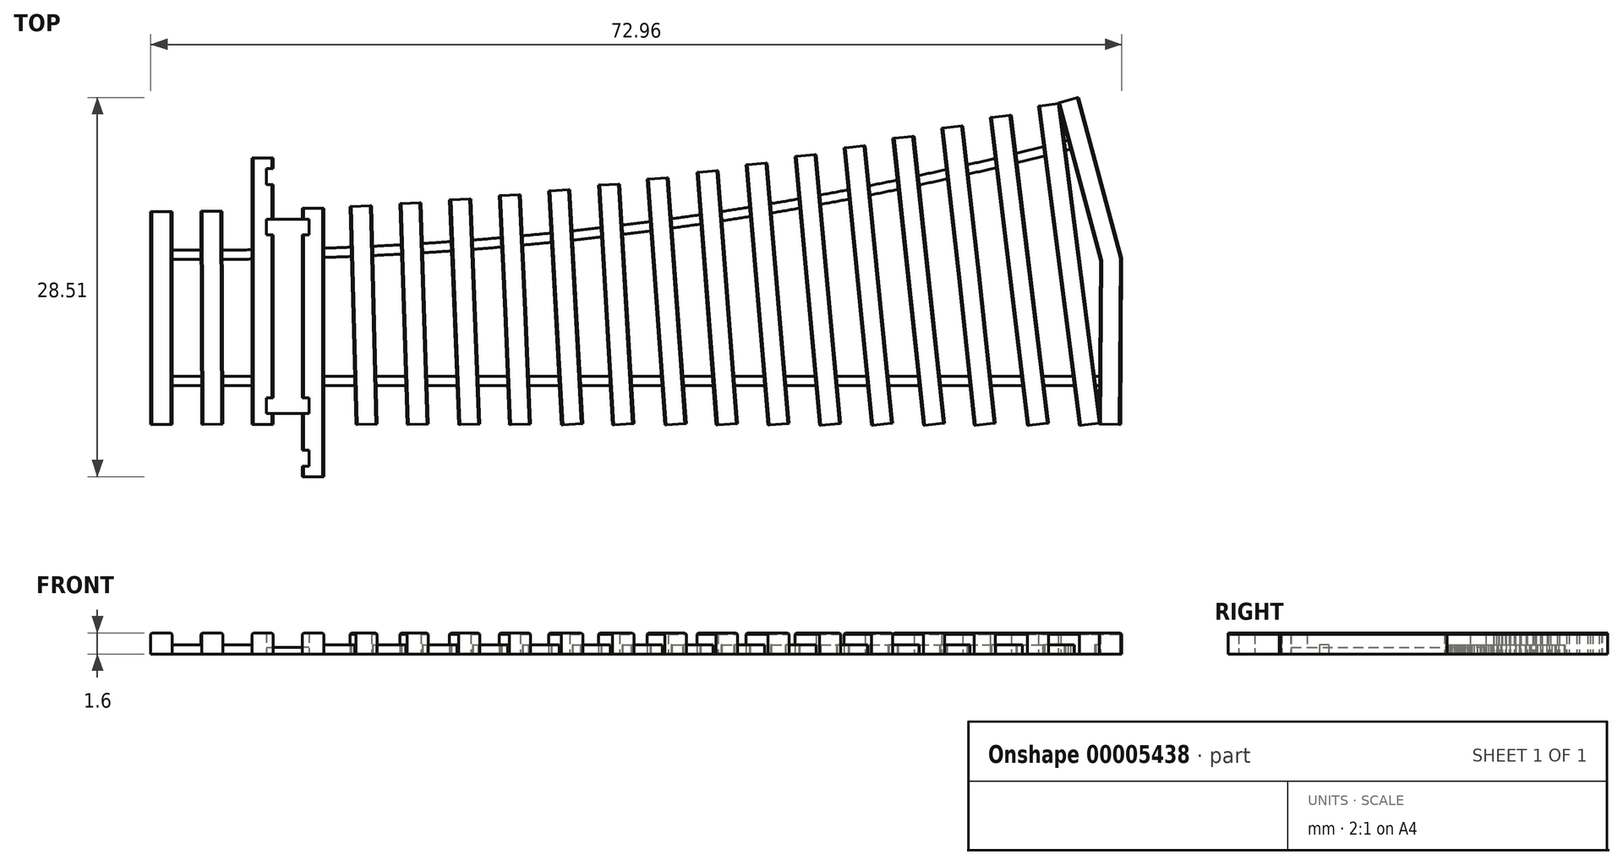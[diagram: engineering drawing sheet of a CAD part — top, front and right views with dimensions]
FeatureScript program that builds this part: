
annotation { "Feature Type Name" : "Feature", "Feature Type Description" : "" }
export const myFeature = defineFeature(function(context is Context, id is Id, definition is map)
    precondition{}
    {
        {
            var Q0;
            Q0=qCreatedBy(makeId("Top.planeOp"),FACE);
            var sketch = newSketch(context, id + "F0", { "sketchPlane" : qUnion([Q0])});
            skLineSegment(sketch, "E0", {"start": v(0, 0) * mm, "end": v(0, 4.5) * mm, "construction": true});
            skLineSegment(sketch, "E1", {"start": v(0, 4.5) * mm, "end": v(-1.16, 8.85) * mm, "construction": true});
            skLineSegment(sketch, "E2", {"start": v(-1.16, 8.85) * mm, "end": v(-34.18, 0) * mm, "construction": true});
            skLineSegment(sketch, "E3", {"start": v(-34.18, 0) * mm, "end": v(0, 0) * mm, "construction": true});
            skLineSegment(sketch, "E4", {"start": v(-34.18, 0) * mm, "end": v(-34.18, 4.5) * mm, "construction": true});
            skLineSegment(sketch, "E5.0.MirrorCS", {"start": v(-34.18, 0) * mm, "end": v(-68.36, 0) * mm, "construction": true});
            skLineSegment(sketch, "E6.0.MirrorCS", {"start": v(0, 0) * mm, "end": v(0, -4.5) * mm, "construction": true});
            skLineSegment(sketch, "E7", {"start": v(0, -4.5) * mm, "end": v(-68.36, -4.5) * mm, "construction": true});
            skLineSegment(sketch, "E8.0.MirrorCS", {"start": v(-2.33, 13.2) * mm, "end": v(-1.16, 8.85) * mm, "construction": true});
            skLineSegment(sketch, "E9", {"start": v(-68.36, 0) * mm, "end": v(-68.36, -4.5) * mm, "construction": true});
            skLineSegment(sketch, "E10.0.MirrorCS", {"start": v(-68.36, 0) * mm, "end": v(-68.36, 4.5) * mm, "construction": true});
            skLineSegment(sketch, "E11", {"start": v(-68.36, 0) * mm, "end": v(-71.36, 0) * mm, "construction": true});
            skArc(sketch, "E12", {"start": v(-68.36, 0) * mm, "mid": v(-34.47, 2.22) * mm, "end": v(-1.16, 8.85) * mm, "construction": true});
            skLineSegment(sketch, "E13", {"start": v(-68.36, -4.5) * mm, "end": v(-71.36, -4.5) * mm, "construction": true});
            skLineSegment(sketch, "E14", {"start": v(-68.36, 4.5) * mm, "end": v(-71.36, 4.5) * mm, "construction": true});
            skArc(sketch, "E15", {"start": v(-68.36, 4.5) * mm, "mid": v(-35.06, 6.68) * mm, "end": v(-2.33, 13.2) * mm, "construction": true});
            skSolve(sketch);
        }
        {
            var Q0;
            Q0=qCreatedBy(makeId("Top.planeOp"),FACE);
            var sketch = newSketch(context, id + "F1", { "sketchPlane" : qUnion([Q0])});
            skPoint(sketch, "E16.0", {"position": v(-68.36, 0) * mm});
            skLineSegment(sketch, "E17.0", {"start": v(-68.36, 0) * mm, "end": v(-72.16, 0) * mm, "construction": true});
            skArc(sketch, "E18", {"start": v(-68.36, 0) * mm, "mid": v(-34.1, 1.13) * mm, "end": v(0, 4.5) * mm, "construction": true});
            skLineSegment(sketch, "E19", {"start": v(-68.36, 0) * mm, "end": v(-64.56, 0.01) * mm, "construction": true});
            skLineSegment(sketch, "E20", {"start": v(-64.56, 0.01) * mm, "end": v(-60.76, 0.06) * mm, "construction": true});
            skLineSegment(sketch, "E21", {"start": v(-60.76, 0.06) * mm, "end": v(-56.96, 0.12) * mm, "construction": true});
            skLineSegment(sketch, "E22", {"start": v(-56.96, 0.12) * mm, "end": v(-53.16, 0.22) * mm, "construction": true});
            skLineSegment(sketch, "E23", {"start": v(-53.16, 0.22) * mm, "end": v(-49.37, 0.35) * mm, "construction": true});
            skLineSegment(sketch, "E24", {"start": v(-49.37, 0.35) * mm, "end": v(-45.57, 0.5) * mm, "construction": true});
            skLineSegment(sketch, "E25", {"start": v(-45.57, 0.5) * mm, "end": v(-41.77, 0.68) * mm, "construction": true});
            skLineSegment(sketch, "E26", {"start": v(-41.77, 0.68) * mm, "end": v(-37.98, 0.89) * mm, "construction": true});
            skLineSegment(sketch, "E27", {"start": v(-37.98, 0.89) * mm, "end": v(-34.19, 1.1) * mm, "construction": true});
            skLineSegment(sketch, "E28", {"start": v(-34.19, 1.1) * mm, "end": v(-30.4, 1.38) * mm, "construction": true});
            skLineSegment(sketch, "E29", {"start": v(-30.4, 1.38) * mm, "end": v(-26.6, 1.67) * mm, "construction": true});
            skLineSegment(sketch, "E30", {"start": v(-26.6, 1.67) * mm, "end": v(-22.82, 2) * mm, "construction": true});
            skLineSegment(sketch, "E31", {"start": v(-22.82, 2) * mm, "end": v(-19.04, 2.34) * mm, "construction": true});
            skLineSegment(sketch, "E32", {"start": v(-19.04, 2.34) * mm, "end": v(-15.25, 2.71) * mm, "construction": true});
            skLineSegment(sketch, "E33", {"start": v(-15.25, 2.71) * mm, "end": v(-11.48, 3.11) * mm, "construction": true});
            skLineSegment(sketch, "E34", {"start": v(-11.48, 3.11) * mm, "end": v(-7.7, 3.54) * mm, "construction": true});
            skLineSegment(sketch, "E35", {"start": v(-7.7, 3.54) * mm, "end": v(-3.93, 4) * mm, "construction": true});
            skLineSegment(sketch, "E36", {"start": v(-3.93, 4) * mm, "end": v(-0.16, 4.48) * mm, "construction": true});
            skLineSegment(sketch, "E37", {"start": v(-72.16, 0) * mm, "end": v(-72.16, 8) * mm, "construction": true});
            skLineSegment(sketch, "E38", {"start": v(-68.36, 0) * mm, "end": v(-68.4, 8.03) * mm, "construction": true});
            skLineSegment(sketch, "E39", {"start": v(-56.96, 0.12) * mm, "end": v(-57.17, 8.4) * mm, "construction": true});
            skLineSegment(sketch, "E40", {"start": v(-53.16, 0.22) * mm, "end": v(-53.44, 8.62) * mm, "construction": true});
            skLineSegment(sketch, "E41", {"start": v(-49.37, 0.35) * mm, "end": v(-49.7, 8.9) * mm, "construction": true});
            skLineSegment(sketch, "E42", {"start": v(-45.57, 0.5) * mm, "end": v(-45.98, 9.22) * mm, "construction": true});
            skLineSegment(sketch, "E43", {"start": v(-41.77, 0.68) * mm, "end": v(-42.26, 9.6) * mm, "construction": true});
            skLineSegment(sketch, "E44", {"start": v(-37.98, 0.89) * mm, "end": v(-38.51, 10.02) * mm, "construction": true});
            skLineSegment(sketch, "E45", {"start": v(-34.19, 1.1) * mm, "end": v(-34.87, 10.48) * mm, "construction": true});
            skLineSegment(sketch, "E46", {"start": v(-30.4, 1.38) * mm, "end": v(-31.13, 11) * mm, "construction": true});
            skLineSegment(sketch, "E47", {"start": v(-26.6, 1.67) * mm, "end": v(-27.44, 11.58) * mm, "construction": true});
            skLineSegment(sketch, "E48", {"start": v(-22.82, 2) * mm, "end": v(-23.75, 12.2) * mm, "construction": true});
            skLineSegment(sketch, "E49", {"start": v(-19.04, 2.34) * mm, "end": v(-20.07, 12.86) * mm, "construction": true});
            skLineSegment(sketch, "E50", {"start": v(-15.25, 2.71) * mm, "end": v(-16.4, 13.58) * mm, "construction": true});
            skLineSegment(sketch, "E51", {"start": v(-11.48, 3.11) * mm, "end": v(-12.75, 14.34) * mm, "construction": true});
            skLineSegment(sketch, "E52", {"start": v(-7.7, 3.54) * mm, "end": v(-9.1, 15.16) * mm, "construction": true});
            skLineSegment(sketch, "E53", {"start": v(-3.93, 4) * mm, "end": v(-5.47, 16.02) * mm, "construction": true});
            skLineSegment(sketch, "E54", {"start": v(-72.16, 8) * mm, "end": v(-73.88, 8) * mm});
            skLineSegment(sketch, "E55.0.MirrorCS", {"start": v(-72.16, 0) * mm, "end": v(-72.16, -8) * mm, "construction": true});
            skLineSegment(sketch, "E56", {"start": v(-72.16, -8) * mm, "end": v(-2.39, -8) * mm, "construction": true});
            skLineSegment(sketch, "E57", {"start": v(-68.36, 0) * mm, "end": v(-68.33, -8) * mm, "construction": true});
            skLineSegment(sketch, "E58", {"start": v(-60.76, 0.06) * mm, "end": v(-60.76, 8.23) * mm, "construction": true});
            skLineSegment(sketch, "E59", {"start": v(-60.76, 0.06) * mm, "end": v(-60.76, -11.94) * mm, "construction": true});
            skLineSegment(sketch, "E60", {"start": v(-64.56, 0.01) * mm, "end": v(-64.56, 12.01) * mm, "construction": true});
            skLineSegment(sketch, "E61", {"start": v(-56.96, 0.12) * mm, "end": v(-56.76, -8) * mm, "construction": true});
            skLineSegment(sketch, "E62", {"start": v(-53.16, 0.22) * mm, "end": v(-52.9, -8) * mm, "construction": true});
            skLineSegment(sketch, "E63", {"start": v(-49.37, 0.35) * mm, "end": v(-49.03, -8) * mm, "construction": true});
            skLineSegment(sketch, "E64", {"start": v(-45.57, 0.5) * mm, "end": v(-45.23, -8) * mm, "construction": true});
            skLineSegment(sketch, "E65", {"start": v(-41.77, 0.68) * mm, "end": v(-41.3, -8) * mm, "construction": true});
            skLineSegment(sketch, "E66", {"start": v(-37.98, 0.89) * mm, "end": v(-37.46, -8) * mm, "construction": true});
            skLineSegment(sketch, "E67", {"start": v(-34.19, 1.1) * mm, "end": v(-33.52, -8) * mm, "construction": true});
            skLineSegment(sketch, "E68", {"start": v(-30.4, 1.38) * mm, "end": v(-29.68, -8) * mm, "construction": true});
            skLineSegment(sketch, "E69", {"start": v(-26.6, 1.67) * mm, "end": v(-25.8, -8) * mm, "construction": true});
            skLineSegment(sketch, "E70", {"start": v(-22.82, 2) * mm, "end": v(-21.9, -8) * mm, "construction": true});
            skLineSegment(sketch, "E71", {"start": v(-19.04, 2.34) * mm, "end": v(-18.02, -8) * mm, "construction": true});
            skLineSegment(sketch, "E72", {"start": v(-15.25, 2.71) * mm, "end": v(-14.12, -8) * mm, "construction": true});
            skLineSegment(sketch, "E73", {"start": v(-11.48, 3.11) * mm, "end": v(-10.3, -8) * mm, "construction": true});
            skLineSegment(sketch, "E74", {"start": v(-7.7, 3.54) * mm, "end": v(-6.3, -8) * mm, "construction": true});
            skLineSegment(sketch, "E75", {"start": v(-3.93, 4) * mm, "end": v(-2.39, -8) * mm, "construction": true});
            skLineSegment(sketch, "E76.0", {"start": v(0, 4.5) * mm, "end": v(-1.16, 8.85) * mm, "construction": true});
            skLineSegment(sketch, "E77", {"start": v(-1.16, 8.85) * mm, "end": v(-3.24, 16.57) * mm, "construction": true});
            skArc(sketch, "E78", {"start": v(-72.16, 8) * mm, "mid": v(-37.43, 10.15) * mm, "end": v(-3.24, 16.57) * mm, "construction": true});
            skLineSegment(sketch, "E79", {"start": v(-64.56, 0.01) * mm, "end": v(-64.56, -8) * mm, "construction": true});
            skLineSegment(sketch, "E80.0.MirrorCS", {"start": v(0, 4.5) * mm, "end": v(-0.03, 0) * mm, "construction": true});
            skLineSegment(sketch, "E81.0.MirrorCS", {"start": v(-0.03, 0) * mm, "end": v(-0.08, -8) * mm, "construction": true});
            skLineSegment(sketch, "E82", {"start": v(-2.39, -8) * mm, "end": v(-0.08, -8) * mm, "construction": true});
            skSolve(sketch);
        }
        {
            var Q0;
            Q0=qCreatedBy(makeId("Top.planeOp"),FACE);
            var sketch = newSketch(context, id + "F2", { "sketchPlane" : qUnion([Q0])});
            skLineSegment(sketch, "E83", {"start": v(-67.6, 8.03) * mm, "end": v(-69.2, 8.02) * mm});
            skLineSegment(sketch, "E84", {"start": v(-69.13, -8) * mm, "end": v(-67.53, -8) * mm});
            skLineSegment(sketch, "E85", {"start": v(-71.36, 8) * mm, "end": v(-72.96, 8) * mm});
            skLineSegment(sketch, "E86", {"start": v(-72.96, -8) * mm, "end": v(-71.36, -8) * mm});
            skLineSegment(sketch, "E87.0", {"start": v(-68.36, 5.1) * mm, "end": v(-68.38, 5.1) * mm});
            skArc(sketch, "E87.1", {"start": v(-67.58, 5.1) * mm, "mid": v(-66.47, 5.1) * mm, "end": v(-65.36, 5.12) * mm});
            skLineSegment(sketch, "E88.0", {"start": v(-68.36, 4.4) * mm, "end": v(-68.38, 4.4) * mm});
            skArc(sketch, "E88.1", {"start": v(-67.58, 4.4) * mm, "mid": v(-66.47, 4.4) * mm, "end": v(-65.36, 4.42) * mm});
            skLineSegment(sketch, "E89.0", {"start": v(-69.15, -4.4) * mm, "end": v(-71.36, -4.4) * mm});
            skLineSegment(sketch, "E89.1", {"start": v(-1.66, -4.4) * mm, "end": v(-2.04, -4.4) * mm});
            skLineSegment(sketch, "E90.0", {"start": v(-69.14, -5.1) * mm, "end": v(-71.36, -5.1) * mm});
            skLineSegment(sketch, "E90.1", {"start": v(-1.66, -5.1) * mm, "end": v(-1.95, -5.1) * mm});
            skLineSegment(sketch, "E91.0", {"start": v(-63.76, 0.01) * mm, "end": v(-63.76, 6.23) * mm});
            skLineSegment(sketch, "E91.1", {"start": v(-63.76, 0.01) * mm, "end": v(-63.76, -6) * mm});
            skLineSegment(sketch, "E92.0", {"start": v(-65.36, 0.01) * mm, "end": v(-65.36, 12.01) * mm});
            skLineSegment(sketch, "E92.1", {"start": v(-65.36, 0.01) * mm, "end": v(-65.36, -8) * mm});
            skLineSegment(sketch, "E93.0", {"start": v(-59.96, 0.06) * mm, "end": v(-59.96, 8.23) * mm});
            skLineSegment(sketch, "E93.1", {"start": v(-59.96, 0.06) * mm, "end": v(-59.96, -11.94) * mm});
            skLineSegment(sketch, "E94.0", {"start": v(-61.56, 0.06) * mm, "end": v(-61.56, 6.23) * mm});
            skLineSegment(sketch, "E94.1", {"start": v(-61.56, 0.06) * mm, "end": v(-61.56, -6) * mm});
            skLineSegment(sketch, "E95", {"start": v(-65.36, 12.01) * mm, "end": v(-63.76, 12.01) * mm});
            skLineSegment(sketch, "E96", {"start": v(-63.76, -8) * mm, "end": v(-65.36, -8) * mm});
            skLineSegment(sketch, "E97", {"start": v(-61.56, -11.94) * mm, "end": v(-59.96, -11.94) * mm});
            skLineSegment(sketch, "E98", {"start": v(-59.96, 8.23) * mm, "end": v(-61.56, 8.23) * mm});
            skPoint(sketch, "E99", {"position": v(-61.35, 8.23) * mm});
            skLineSegment(sketch, "E100", {"start": v(-61.56, 7.43) * mm, "end": v(-61.06, 7.43) * mm});
            skLineSegment(sketch, "E101", {"start": v(-61.06, 7.43) * mm, "end": v(-61.06, 6.23) * mm});
            skLineSegment(sketch, "E102", {"start": v(-61.06, 6.23) * mm, "end": v(-61.56, 6.23) * mm});
            skLineSegment(sketch, "E103", {"start": v(-63.76, 7.43) * mm, "end": v(-64.26, 7.43) * mm});
            skLineSegment(sketch, "E104", {"start": v(-64.26, 7.43) * mm, "end": v(-64.26, 6.23) * mm});
            skLineSegment(sketch, "E105", {"start": v(-64.26, 6.23) * mm, "end": v(-63.76, 6.23) * mm});
            skLineSegment(sketch, "E106", {"start": v(-63.76, 7.43) * mm, "end": v(-61.56, 7.43) * mm});
            skLineSegment(sketch, "E107.trimOffspring", {"start": v(-63.76, 7.43) * mm, "end": v(-63.76, 10.01) * mm});
            skLineSegment(sketch, "E108.trimOffspring", {"start": v(-61.56, 7.43) * mm, "end": v(-61.56, 8.23) * mm});
            skArc(sketch, "E109.trimOffspring", {"start": v(-59.96, 5.24) * mm, "mid": v(-58.93, 5.27) * mm, "end": v(-57.9, 5.32) * mm});
            skArc(sketch, "E110.trimOffspring", {"start": v(-59.96, 4.54) * mm, "mid": v(-58.92, 4.57) * mm, "end": v(-57.88, 4.62) * mm});
            skLineSegment(sketch, "E111.trimOffspring", {"start": v(-69.18, 5.1) * mm, "end": v(-71.36, 5.1) * mm});
            skLineSegment(sketch, "E112.trimOffspring", {"start": v(-69.18, 4.4) * mm, "end": v(-71.36, 4.4) * mm});
            skLineSegment(sketch, "E113.0", {"start": v(-56.16, 0.14) * mm, "end": v(-56.37, 8.42) * mm});
            skLineSegment(sketch, "E113.1", {"start": v(-56.16, 0.14) * mm, "end": v(-55.96, -7.98) * mm});
            skLineSegment(sketch, "E114.0", {"start": v(-57.76, 0.1) * mm, "end": v(-57.56, -8.02) * mm});
            skLineSegment(sketch, "E114.1", {"start": v(-57.76, 0.1) * mm, "end": v(-57.97, 8.38) * mm});
            skLineSegment(sketch, "E115.0", {"start": v(-52.36, 0.25) * mm, "end": v(-52.64, 8.65) * mm});
            skLineSegment(sketch, "E115.1", {"start": v(-52.36, 0.25) * mm, "end": v(-52.1, -7.97) * mm});
            skLineSegment(sketch, "E116.0", {"start": v(-53.96, 0.2) * mm, "end": v(-53.7, -8.03) * mm});
            skLineSegment(sketch, "E116.1", {"start": v(-53.96, 0.2) * mm, "end": v(-54.24, 8.6) * mm});
            skLineSegment(sketch, "E117.0", {"start": v(-48.57, 0.38) * mm, "end": v(-48.9, 8.93) * mm});
            skLineSegment(sketch, "E117.1", {"start": v(-48.57, 0.38) * mm, "end": v(-48.23, -7.97) * mm});
            skLineSegment(sketch, "E118.0", {"start": v(-50.17, 0.31) * mm, "end": v(-49.83, -8.03) * mm});
            skLineSegment(sketch, "E118.1", {"start": v(-50.17, 0.31) * mm, "end": v(-50.5, 8.87) * mm});
            skLineSegment(sketch, "E119.0", {"start": v(-40.97, 0.72) * mm, "end": v(-41.46, 9.64) * mm});
            skLineSegment(sketch, "E119.1", {"start": v(-40.97, 0.72) * mm, "end": v(-40.5, -7.96) * mm});
            skLineSegment(sketch, "E120.0", {"start": v(-42.57, 0.63) * mm, "end": v(-42.1, -8.04) * mm});
            skLineSegment(sketch, "E120.1", {"start": v(-42.57, 0.63) * mm, "end": v(-43.06, 9.55) * mm});
            skLineSegment(sketch, "E121", {"start": v(-57.97, 8.38) * mm, "end": v(-56.37, 8.42) * mm});
            skLineSegment(sketch, "E122", {"start": v(-54.24, 8.6) * mm, "end": v(-52.64, 8.65) * mm});
            skLineSegment(sketch, "E123", {"start": v(-50.5, 8.87) * mm, "end": v(-48.9, 8.93) * mm});
            skLineSegment(sketch, "E124", {"start": v(-46.78, 9.18) * mm, "end": v(-45.18, 9.26) * mm});
            skLineSegment(sketch, "E125", {"start": v(-43.06, 9.55) * mm, "end": v(-41.46, 9.64) * mm});
            skLineSegment(sketch, "E126", {"start": v(-57.56, -8.02) * mm, "end": v(-55.96, -7.98) * mm});
            skLineSegment(sketch, "E127", {"start": v(-53.7, -8.03) * mm, "end": v(-52.1, -7.97) * mm});
            skLineSegment(sketch, "E128", {"start": v(-49.83, -8.03) * mm, "end": v(-48.23, -7.97) * mm});
            skLineSegment(sketch, "E129", {"start": v(-46.03, -8.03) * mm, "end": v(-44.43, -7.97) * mm});
            skLineSegment(sketch, "E130", {"start": v(-42.1, -8.04) * mm, "end": v(-40.5, -7.96) * mm});
            skArc(sketch, "E131.trimOffspring", {"start": v(-56.3, 5.39) * mm, "mid": v(-55.22, 5.44) * mm, "end": v(-54.14, 5.5) * mm});
            skArc(sketch, "E132.trimOffspring", {"start": v(-56.28, 4.69) * mm, "mid": v(-55.2, 4.74) * mm, "end": v(-54.11, 4.8) * mm});
            skArc(sketch, "E133.trimOffspring", {"start": v(-52.54, 5.6) * mm, "mid": v(-51.46, 5.66) * mm, "end": v(-50.38, 5.74) * mm});
            skArc(sketch, "E134.trimOffspring", {"start": v(-52.52, 4.9) * mm, "mid": v(-51.44, 4.96) * mm, "end": v(-50.35, 5.04) * mm});
            skArc(sketch, "E135.trimOffspring", {"start": v(-48.79, 5.85) * mm, "mid": v(-47.7, 5.94) * mm, "end": v(-46.63, 6.03) * mm});
            skArc(sketch, "E136.trimOffspring", {"start": v(-48.76, 5.15) * mm, "mid": v(-47.68, 5.24) * mm, "end": v(-46.6, 5.33) * mm});
            skArc(sketch, "E137.trimOffspring", {"start": v(-45.04, 6.17) * mm, "mid": v(-43.96, 6.27) * mm, "end": v(-42.89, 6.38) * mm});
            skArc(sketch, "E138.trimOffspring", {"start": v(-45, 5.47) * mm, "mid": v(-43.93, 5.57) * mm, "end": v(-42.85, 5.68) * mm});
            skArc(sketch, "E139.trimOffspring", {"start": v(-41.3, 6.54) * mm, "mid": v(-40.2, 6.66) * mm, "end": v(-39.12, 6.78) * mm});
            skArc(sketch, "E140.trimOffspring", {"start": v(-41.25, 5.84) * mm, "mid": v(-40.17, 5.96) * mm, "end": v(-39.08, 6.08) * mm});
            skLineSegment(sketch, "E141.trimOffspring", {"start": v(-65.36, -4.4) * mm, "end": v(-67.55, -4.4) * mm});
            skLineSegment(sketch, "E142.trimOffspring", {"start": v(-65.36, -5.1) * mm, "end": v(-67.54, -5.1) * mm});
            skLineSegment(sketch, "E143.trimOffspring", {"start": v(-57.65, -4.4) * mm, "end": v(-59.96, -4.4) * mm});
            skLineSegment(sketch, "E144.trimOffspring", {"start": v(-57.63, -5.1) * mm, "end": v(-59.96, -5.1) * mm});
            skLineSegment(sketch, "E145.trimOffspring", {"start": v(-53.81, -4.4) * mm, "end": v(-56.05, -4.4) * mm});
            skLineSegment(sketch, "E146.trimOffspring", {"start": v(-53.79, -5.1) * mm, "end": v(-56.03, -5.1) * mm});
            skLineSegment(sketch, "E147.trimOffspring", {"start": v(-49.98, -4.4) * mm, "end": v(-52.21, -4.4) * mm});
            skLineSegment(sketch, "E148.trimOffspring", {"start": v(-49.95, -5.1) * mm, "end": v(-52.19, -5.1) * mm});
            skLineSegment(sketch, "E149.trimOffspring", {"start": v(-46.17, -4.4) * mm, "end": v(-48.37, -4.4) * mm});
            skLineSegment(sketch, "E150.trimOffspring", {"start": v(-46.15, -5.1) * mm, "end": v(-48.35, -5.1) * mm});
            skLineSegment(sketch, "E151.trimOffspring", {"start": v(-42.3, -4.4) * mm, "end": v(-44.57, -4.4) * mm});
            skLineSegment(sketch, "E152.trimOffspring", {"start": v(-42.26, -5.1) * mm, "end": v(-44.54, -5.1) * mm});
            skLineSegment(sketch, "E153.0", {"start": v(-37.18, 0.93) * mm, "end": v(-37.71, 10.07) * mm});
            skLineSegment(sketch, "E153.1", {"start": v(-37.18, 0.93) * mm, "end": v(-36.66, -7.95) * mm});
            skLineSegment(sketch, "E154.0", {"start": v(-38.78, 0.84) * mm, "end": v(-38.26, -8.05) * mm});
            skLineSegment(sketch, "E154.1", {"start": v(-38.78, 0.84) * mm, "end": v(-39.31, 9.97) * mm});
            skLineSegment(sketch, "E155.0", {"start": v(-33.39, 1.17) * mm, "end": v(-34.07, 10.54) * mm});
            skLineSegment(sketch, "E155.1", {"start": v(-33.39, 1.17) * mm, "end": v(-32.72, -7.94) * mm});
            skLineSegment(sketch, "E156.0", {"start": v(-34.98, 1.05) * mm, "end": v(-34.32, -8.06) * mm});
            skLineSegment(sketch, "E156.1", {"start": v(-34.98, 1.05) * mm, "end": v(-35.67, 10.42) * mm});
            skLineSegment(sketch, "E157.0", {"start": v(-29.6, 1.44) * mm, "end": v(-30.34, 11.07) * mm});
            skLineSegment(sketch, "E157.1", {"start": v(-29.6, 1.44) * mm, "end": v(-28.88, -7.94) * mm});
            skLineSegment(sketch, "E158.0", {"start": v(-31.2, 1.32) * mm, "end": v(-30.47, -8.06) * mm});
            skLineSegment(sketch, "E158.1", {"start": v(-31.2, 1.32) * mm, "end": v(-31.93, 10.95) * mm});
            skLineSegment(sketch, "E159.0", {"start": v(-25.8, 1.74) * mm, "end": v(-26.64, 11.64) * mm});
            skLineSegment(sketch, "E159.1", {"start": v(-25.8, 1.74) * mm, "end": v(-25, -7.93) * mm});
            skLineSegment(sketch, "E160.0", {"start": v(-27.4, 1.6) * mm, "end": v(-26.6, -8.07) * mm});
            skLineSegment(sketch, "E160.1", {"start": v(-27.4, 1.6) * mm, "end": v(-28.24, 11.51) * mm});
            skLineSegment(sketch, "E161.0", {"start": v(-22.02, 2.07) * mm, "end": v(-22.96, 12.27) * mm});
            skLineSegment(sketch, "E161.1", {"start": v(-22.02, 2.07) * mm, "end": v(-21.11, -7.93) * mm});
            skLineSegment(sketch, "E162.0", {"start": v(-23.62, 1.92) * mm, "end": v(-22.7, -8.07) * mm});
            skLineSegment(sketch, "E162.1", {"start": v(-23.62, 1.92) * mm, "end": v(-24.55, 12.12) * mm});
            skLineSegment(sketch, "E163.0", {"start": v(-18.24, 2.42) * mm, "end": v(-19.28, 12.94) * mm});
            skLineSegment(sketch, "E163.1", {"start": v(-18.24, 2.42) * mm, "end": v(-17.22, -7.92) * mm});
            skLineSegment(sketch, "E164.0", {"start": v(-19.83, 2.26) * mm, "end": v(-18.81, -8.08) * mm});
            skLineSegment(sketch, "E164.1", {"start": v(-19.83, 2.26) * mm, "end": v(-20.87, 12.79) * mm});
            skLineSegment(sketch, "E165.0", {"start": v(-14.46, 2.8) * mm, "end": v(-15.61, 13.66) * mm});
            skLineSegment(sketch, "E165.1", {"start": v(-14.46, 2.8) * mm, "end": v(-13.32, -7.92) * mm});
            skLineSegment(sketch, "E166.0", {"start": v(-16.05, 2.63) * mm, "end": v(-14.91, -8.08) * mm});
            skLineSegment(sketch, "E166.1", {"start": v(-16.05, 2.63) * mm, "end": v(-17.2, 13.5) * mm});
            skLineSegment(sketch, "E167.0", {"start": v(-10.68, 3.2) * mm, "end": v(-11.95, 14.44) * mm});
            skLineSegment(sketch, "E167.1", {"start": v(-10.68, 3.2) * mm, "end": v(-9.5, -7.92) * mm});
            skLineSegment(sketch, "E168.0", {"start": v(-12.27, 3.02) * mm, "end": v(-11.1, -8.08) * mm});
            skLineSegment(sketch, "E168.1", {"start": v(-12.27, 3.02) * mm, "end": v(-13.54, 14.25) * mm});
            skLineSegment(sketch, "E169.0", {"start": v(-6.9, 3.64) * mm, "end": v(-8.3, 15.25) * mm});
            skLineSegment(sketch, "E169.1", {"start": v(-6.9, 3.64) * mm, "end": v(-5.51, -7.9) * mm});
            skLineSegment(sketch, "E170.0", {"start": v(-8.5, 3.44) * mm, "end": v(-7.1, -8.1) * mm});
            skLineSegment(sketch, "E170.1", {"start": v(-8.5, 3.44) * mm, "end": v(-9.9, 15.06) * mm});
            skLineSegment(sketch, "E171.0", {"start": v(-3.13, 4.1) * mm, "end": v(-4.59, 15.44) * mm});
            skLineSegment(sketch, "E171.1", {"start": v(-3.13, 4.1) * mm, "end": v(-1.68, -7.24) * mm});
            skLineSegment(sketch, "E172.0", {"start": v(-4.72, 3.9) * mm, "end": v(-3.18, -8.1) * mm});
            skLineSegment(sketch, "E172.1", {"start": v(-4.72, 3.9) * mm, "end": v(-6.26, 15.92) * mm});
            skLineSegment(sketch, "E173", {"start": v(-39.31, 9.97) * mm, "end": v(-37.71, 10.07) * mm});
            skLineSegment(sketch, "E174", {"start": v(-35.67, 10.42) * mm, "end": v(-34.07, 10.54) * mm});
            skLineSegment(sketch, "E175", {"start": v(-31.93, 10.95) * mm, "end": v(-30.34, 11.07) * mm});
            skLineSegment(sketch, "E176", {"start": v(-28.24, 11.51) * mm, "end": v(-26.64, 11.64) * mm});
            skLineSegment(sketch, "E177", {"start": v(-38.26, -8.05) * mm, "end": v(-36.66, -7.95) * mm});
            skLineSegment(sketch, "E178", {"start": v(-34.32, -8.06) * mm, "end": v(-32.72, -7.94) * mm});
            skLineSegment(sketch, "E179", {"start": v(-30.47, -8.06) * mm, "end": v(-28.88, -7.94) * mm});
            skLineSegment(sketch, "E180", {"start": v(-26.6, -8.07) * mm, "end": v(-25, -7.93) * mm});
            skLineSegment(sketch, "E181", {"start": v(-22.7, -8.07) * mm, "end": v(-21.11, -7.93) * mm});
            skLineSegment(sketch, "E182", {"start": v(-18.81, -8.08) * mm, "end": v(-17.22, -7.92) * mm});
            skLineSegment(sketch, "E183", {"start": v(-14.91, -8.08) * mm, "end": v(-13.32, -7.92) * mm});
            skLineSegment(sketch, "E184", {"start": v(-11.1, -8.08) * mm, "end": v(-9.5, -7.92) * mm});
            skLineSegment(sketch, "E185", {"start": v(-24.55, 12.12) * mm, "end": v(-22.96, 12.27) * mm});
            skLineSegment(sketch, "E186", {"start": v(-20.87, 12.79) * mm, "end": v(-19.28, 12.94) * mm});
            skLineSegment(sketch, "E187", {"start": v(-17.2, 13.5) * mm, "end": v(-15.61, 13.66) * mm});
            skLineSegment(sketch, "E188", {"start": v(-13.54, 14.25) * mm, "end": v(-11.95, 14.44) * mm});
            skLineSegment(sketch, "E189", {"start": v(-9.9, 15.06) * mm, "end": v(-8.3, 15.25) * mm});
            skLineSegment(sketch, "E190", {"start": v(-7.1, -8.1) * mm, "end": v(-5.51, -7.9) * mm});
            skLineSegment(sketch, "E191", {"start": v(-4.77, 16.1) * mm, "end": v(-6.26, 15.92) * mm});
            skLineSegment(sketch, "E192", {"start": v(-3.18, -8.1) * mm, "end": v(-1.68, -7.9) * mm});
            skArc(sketch, "E193.trimOffspring", {"start": v(-37.53, 6.97) * mm, "mid": v(-36.48, 7.1) * mm, "end": v(-35.44, 7.24) * mm});
            skArc(sketch, "E194.trimOffspring", {"start": v(-37.5, 6.27) * mm, "mid": v(-36.44, 6.4) * mm, "end": v(-35.38, 6.54) * mm});
            skArc(sketch, "E195.trimOffspring", {"start": v(-33.85, 7.45) * mm, "mid": v(-32.77, 7.6) * mm, "end": v(-31.69, 7.76) * mm});
            skArc(sketch, "E196.trimOffspring", {"start": v(-33.8, 6.75) * mm, "mid": v(-32.71, 6.9) * mm, "end": v(-31.63, 7.06) * mm});
            skArc(sketch, "E197.trimOffspring", {"start": v(-30.1, 8) * mm, "mid": v(-29.03, 8.16) * mm, "end": v(-27.97, 8.33) * mm});
            skArc(sketch, "E198.trimOffspring", {"start": v(-30.05, 7.3) * mm, "mid": v(-28.98, 7.46) * mm, "end": v(-27.9, 7.63) * mm});
            skArc(sketch, "E199.trimOffspring", {"start": v(-26.38, 8.59) * mm, "mid": v(-25.32, 8.77) * mm, "end": v(-24.26, 8.95) * mm});
            skArc(sketch, "E200.trimOffspring", {"start": v(-26.33, 7.89) * mm, "mid": v(-25.26, 8.07) * mm, "end": v(-24.2, 8.25) * mm});
            skArc(sketch, "E201.trimOffspring", {"start": v(-22.68, 9.23) * mm, "mid": v(-21.62, 9.43) * mm, "end": v(-20.56, 9.63) * mm});
            skArc(sketch, "E202.trimOffspring", {"start": v(-22.61, 8.53) * mm, "mid": v(-21.55, 8.73) * mm, "end": v(-20.5, 8.93) * mm});
            skArc(sketch, "E203.trimOffspring", {"start": v(-18.98, 9.94) * mm, "mid": v(-17.93, 10.15) * mm, "end": v(-16.87, 10.36) * mm});
            skArc(sketch, "E204.trimOffspring", {"start": v(-18.91, 9.24) * mm, "mid": v(-17.85, 9.45) * mm, "end": v(-16.8, 9.66) * mm});
            skLineSegment(sketch, "E205.trimOffspring", {"start": v(-38.47, -4.4) * mm, "end": v(-40.7, -4.4) * mm});
            skLineSegment(sketch, "E206.trimOffspring", {"start": v(-38.43, -5.1) * mm, "end": v(-40.66, -5.1) * mm});
            skLineSegment(sketch, "E207.trimOffspring", {"start": v(-34.59, -4.4) * mm, "end": v(-36.87, -4.4) * mm});
            skLineSegment(sketch, "E208.trimOffspring", {"start": v(-34.53, -5.1) * mm, "end": v(-36.83, -5.1) * mm});
            skLineSegment(sketch, "E209.trimOffspring", {"start": v(-30.75, -4.4) * mm, "end": v(-32.98, -4.4) * mm});
            skLineSegment(sketch, "E210.trimOffspring", {"start": v(-30.7, -5.1) * mm, "end": v(-32.93, -5.1) * mm});
            skLineSegment(sketch, "E211.trimOffspring", {"start": v(-26.9, -4.4) * mm, "end": v(-29.15, -4.4) * mm});
            skLineSegment(sketch, "E212.trimOffspring", {"start": v(-26.84, -5.1) * mm, "end": v(-29.1, -5.1) * mm});
            skLineSegment(sketch, "E213.trimOffspring", {"start": v(-23.04, -4.4) * mm, "end": v(-25.3, -4.4) * mm});
            skLineSegment(sketch, "E214.trimOffspring", {"start": v(-22.98, -5.1) * mm, "end": v(-25.23, -5.1) * mm});
            skLineSegment(sketch, "E215.trimOffspring", {"start": v(-19.17, -4.4) * mm, "end": v(-21.43, -4.4) * mm});
            skLineSegment(sketch, "E216.trimOffspring", {"start": v(-19.1, -5.1) * mm, "end": v(-21.37, -5.1) * mm});
            skArc(sketch, "E217.trimOffspring", {"start": v(-15.3, 10.7) * mm, "mid": v(-14.24, 10.92) * mm, "end": v(-13.2, 11.15) * mm});
            skArc(sketch, "E218.trimOffspring", {"start": v(-15.22, 10) * mm, "mid": v(-14.17, 10.22) * mm, "end": v(-13.11, 10.45) * mm});
            skArc(sketch, "E219.trimOffspring", {"start": v(-11.62, 11.5) * mm, "mid": v(-10.57, 11.75) * mm, "end": v(-9.53, 12) * mm});
            skArc(sketch, "E220.trimOffspring", {"start": v(-11.54, 10.8) * mm, "mid": v(-10.5, 11.05) * mm, "end": v(-9.44, 11.3) * mm});
            skArc(sketch, "E221.trimOffspring", {"start": v(-7.96, 12.37) * mm, "mid": v(-6.92, 12.63) * mm, "end": v(-5.87, 12.89) * mm});
            skArc(sketch, "E222.trimOffspring", {"start": v(-7.88, 11.67) * mm, "mid": v(-6.83, 11.93) * mm, "end": v(-5.78, 12.2) * mm});
            skArc(sketch, "E223.trimOffspring", {"start": v(-4.31, 13.3) * mm, "mid": v(-4.17, 13.33) * mm, "end": v(-4.03, 13.36) * mm});
            skArc(sketch, "E224.trimOffspring", {"start": v(-4.22, 12.6) * mm, "mid": v(-4.04, 12.64) * mm, "end": v(-3.85, 12.69) * mm});
            skLineSegment(sketch, "E225.trimOffspring", {"start": v(-3.66, -4.4) * mm, "end": v(-5.93, -4.4) * mm});
            skLineSegment(sketch, "E226.trimOffspring", {"start": v(-3.57, -5.1) * mm, "end": v(-5.85, -5.1) * mm});
            skLineSegment(sketch, "E227.trimOffspring", {"start": v(-7.55, -4.4) * mm, "end": v(-9.87, -4.4) * mm});
            skLineSegment(sketch, "E228.trimOffspring", {"start": v(-7.46, -5.1) * mm, "end": v(-9.8, -5.1) * mm});
            skLineSegment(sketch, "E229.trimOffspring", {"start": v(-11.48, -4.4) * mm, "end": v(-13.7, -4.4) * mm});
            skLineSegment(sketch, "E230.trimOffspring", {"start": v(-11.4, -5.1) * mm, "end": v(-13.62, -5.1) * mm});
            skLineSegment(sketch, "E231.trimOffspring", {"start": v(-15.3, -4.4) * mm, "end": v(-17.57, -4.4) * mm});
            skLineSegment(sketch, "E232.trimOffspring", {"start": v(-15.23, -5.1) * mm, "end": v(-17.5, -5.1) * mm});
            skPoint(sketch, "E233", {"position": v(-63.94, 12.01) * mm});
            skLineSegment(sketch, "E234", {"start": v(-63.76, 11.21) * mm, "end": v(-64.26, 11.21) * mm});
            skLineSegment(sketch, "E235", {"start": v(-64.26, 11.21) * mm, "end": v(-64.26, 10.01) * mm});
            skLineSegment(sketch, "E236", {"start": v(-64.26, 10.01) * mm, "end": v(-63.76, 10.01) * mm});
            skLineSegment(sketch, "E237.0", {"start": v(-71.36, 0) * mm, "end": v(-71.36, 8) * mm});
            skLineSegment(sketch, "E237.1", {"start": v(-71.36, 0) * mm, "end": v(-71.36, -8) * mm});
            skLineSegment(sketch, "E238.0", {"start": v(-72.96, 0) * mm, "end": v(-72.96, -8) * mm});
            skLineSegment(sketch, "E238.1", {"start": v(-72.96, 0) * mm, "end": v(-72.96, 8) * mm});
            skLineSegment(sketch, "E239.0", {"start": v(-67.56, 0) * mm, "end": v(-67.6, 8.03) * mm});
            skLineSegment(sketch, "E239.1", {"start": v(-67.56, 0) * mm, "end": v(-67.53, -8) * mm});
            skLineSegment(sketch, "E240.0", {"start": v(-69.16, 0) * mm, "end": v(-69.13, -8) * mm});
            skLineSegment(sketch, "E240.1", {"start": v(-69.16, 0) * mm, "end": v(-69.2, 8.02) * mm});
            skLineSegment(sketch, "E241", {"start": v(-63.76, -7.2) * mm, "end": v(-64.26, -7.2) * mm});
            skLineSegment(sketch, "E242", {"start": v(-64.26, -7.2) * mm, "end": v(-64.26, -6) * mm});
            skLineSegment(sketch, "E243", {"start": v(-64.26, -6) * mm, "end": v(-63.76, -6) * mm});
            skLineSegment(sketch, "E244", {"start": v(-61.56, -11.14) * mm, "end": v(-61.06, -11.14) * mm});
            skLineSegment(sketch, "E245", {"start": v(-61.06, -11.14) * mm, "end": v(-61.06, -9.94) * mm});
            skLineSegment(sketch, "E246", {"start": v(-61.06, -9.94) * mm, "end": v(-61.56, -9.94) * mm});
            skLineSegment(sketch, "E247.trimOffspring", {"start": v(-63.76, -7.2) * mm, "end": v(-63.76, -8) * mm});
            skLineSegment(sketch, "E248.trimOffspring", {"start": v(-61.56, -11.14) * mm, "end": v(-61.56, -11.94) * mm});
            skLineSegment(sketch, "E249.trimOffspring", {"start": v(-63.76, 11.21) * mm, "end": v(-63.76, 12.01) * mm});
            skLineSegment(sketch, "E250", {"start": v(-61.56, -7.2) * mm, "end": v(-61.06, -7.2) * mm});
            skLineSegment(sketch, "E251", {"start": v(-61.06, -7.2) * mm, "end": v(-61.06, -6) * mm});
            skLineSegment(sketch, "E252", {"start": v(-61.06, -6) * mm, "end": v(-61.56, -6) * mm});
            skLineSegment(sketch, "E253.trimOffspring", {"start": v(-61.56, -7.2) * mm, "end": v(-61.56, -9.94) * mm});
            skLineSegment(sketch, "E254", {"start": v(-63.76, -7.2) * mm, "end": v(-61.56, -7.2) * mm});
            skLineSegment(sketch, "E255.0", {"start": v(-1.63, 0) * mm, "end": v(-1.68, -8) * mm});
            skLineSegment(sketch, "E255.1", {"start": v(-1.6, 4.3) * mm, "end": v(-1.63, 0) * mm});
            skLineSegment(sketch, "E255.2", {"start": v(-1.6, 4.3) * mm, "end": v(-2.71, 8.43) * mm});
            skLineSegment(sketch, "E255.3", {"start": v(-2.71, 8.43) * mm, "end": v(-4.78, 16.16) * mm});
            skLineSegment(sketch, "E256.0", {"start": v(-0.03, 0) * mm, "end": v(-0.08, -8) * mm});
            skLineSegment(sketch, "E256.1", {"start": v(0, 4.5) * mm, "end": v(-0.03, 0) * mm});
            skLineSegment(sketch, "E256.2", {"start": v(0, 4.5) * mm, "end": v(-1.16, 8.85) * mm});
            skLineSegment(sketch, "E256.3", {"start": v(-1.16, 8.85) * mm, "end": v(-3.24, 16.57) * mm});
            skLineSegment(sketch, "E257", {"start": v(-4.78, 16.16) * mm, "end": v(-3.24, 16.57) * mm});
            skLineSegment(sketch, "E258", {"start": v(-0.08, -8) * mm, "end": v(-1.68, -8) * mm});
            skLineSegment(sketch, "E259.0", {"start": v(-46.37, 0.46) * mm, "end": v(-46.03, -8.03) * mm});
            skLineSegment(sketch, "E259.1", {"start": v(-46.37, 0.46) * mm, "end": v(-46.78, 9.18) * mm});
            skLineSegment(sketch, "E260.0", {"start": v(-44.77, 0.53) * mm, "end": v(-45.18, 9.26) * mm});
            skLineSegment(sketch, "E260.1", {"start": v(-44.77, 0.53) * mm, "end": v(-44.43, -7.97) * mm});
            skSolve(sketch);
        }
        {
            var Q0;
            Q0=makeQuery(id+"F2.imprint","IMPRINT",FACE,{"disambiguationData":[TD([[makeQuery(id+"F2.imprint","IMPRINT",EDGE,{"derivedFrom":sQuery(id+"F2.wireOp",EDGE,"E91.0")}),-1.0]])]});
            extrude(context, id + "F3", {"entities" : qUnion([Q0]), "depth" : 0.5 * mm});
        }
        {
            var Q0;
            Q0=makeQuery(id+"F2.imprint","IMPRINT",FACE,{"disambiguationData":[TD([[makeQuery(id+"F2.imprint","IMPRINT",EDGE,{"derivedFrom":sQuery(id+"F2.wireOp",EDGE,"E91.0")}),1.0]])]});
            var Q1;
            Q1=makeQuery(id+"F2.imprint","IMPRINT",FACE,{"disambiguationData":[TD([[makeQuery(id+"F2.imprint","IMPRINT",EDGE,{"derivedFrom":sQuery(id+"F2.wireOp",EDGE,"E94.0")}),-1.0]])]});
            var Q2;
            {var subQ10=sQuery(id+"F2.wireOp",EDGE,"E83");Q2=makeQuery(id+"F2.imprint","IMPRINT",FACE,{"disambiguationData":[TD([[makeQuery(id+"F2.imprint","IMPRINT",EDGE,{"derivedFrom":subQ10}),1.0]])]});}
            var Q3;
            {var subQ6=sQuery(id+"F2.wireOp",EDGE,"E85");Q3=makeQuery(id+"F2.imprint","IMPRINT",FACE,{"disambiguationData":[TD([[makeQuery(id+"F2.imprint","IMPRINT",EDGE,{"derivedFrom":subQ6}),1.0]])]});}
            var Q4;
            {var subQ1=sQuery(id+"F2.wireOp",EDGE,"E121");Q4=makeQuery(id+"F2.imprint","IMPRINT",FACE,{"disambiguationData":[TD([[makeQuery(id+"F2.imprint","IMPRINT",EDGE,{"derivedFrom":subQ1}),-1.0]])]});}
            var Q5;
            {var subQ0=sQuery(id+"F2.wireOp",EDGE,"E122");Q5=makeQuery(id+"F2.imprint","IMPRINT",FACE,{"disambiguationData":[TD([[makeQuery(id+"F2.imprint","IMPRINT",EDGE,{"derivedFrom":subQ0}),-1.0]])]});}
            var Q6;
            {var subQ2=sQuery(id+"F2.wireOp",EDGE,"E123");Q6=makeQuery(id+"F2.imprint","IMPRINT",FACE,{"disambiguationData":[TD([[makeQuery(id+"F2.imprint","IMPRINT",EDGE,{"derivedFrom":subQ2}),-1.0]])]});}
            var Q7;
            {var subQ3=sQuery(id+"F2.wireOp",EDGE,"E124");Q7=makeQuery(id+"F2.imprint","IMPRINT",FACE,{"disambiguationData":[TD([[makeQuery(id+"F2.imprint","IMPRINT",EDGE,{"derivedFrom":subQ3}),-1.0]])]});}
            var Q8;
            {var subQ3=sQuery(id+"F2.wireOp",EDGE,"E125");Q8=makeQuery(id+"F2.imprint","IMPRINT",FACE,{"disambiguationData":[TD([[makeQuery(id+"F2.imprint","IMPRINT",EDGE,{"derivedFrom":subQ3}),-1.0]])]});}
            var Q9;
            {var subQ1=sQuery(id+"F2.wireOp",EDGE,"E173");Q9=makeQuery(id+"F2.imprint","IMPRINT",FACE,{"disambiguationData":[TD([[makeQuery(id+"F2.imprint","IMPRINT",EDGE,{"derivedFrom":subQ1}),-1.0]])]});}
            var Q10;
            {var subQ1=sQuery(id+"F2.wireOp",EDGE,"E174");Q10=makeQuery(id+"F2.imprint","IMPRINT",FACE,{"disambiguationData":[TD([[makeQuery(id+"F2.imprint","IMPRINT",EDGE,{"derivedFrom":subQ1}),-1.0]])]});}
            var Q11;
            {var subQ2=sQuery(id+"F2.wireOp",EDGE,"E175");Q11=makeQuery(id+"F2.imprint","IMPRINT",FACE,{"disambiguationData":[TD([[makeQuery(id+"F2.imprint","IMPRINT",EDGE,{"derivedFrom":subQ2}),-1.0]])]});}
            var Q12;
            {var subQ2=sQuery(id+"F2.wireOp",EDGE,"E176");Q12=makeQuery(id+"F2.imprint","IMPRINT",FACE,{"disambiguationData":[TD([[makeQuery(id+"F2.imprint","IMPRINT",EDGE,{"derivedFrom":subQ2}),-1.0]])]});}
            var Q13;
            {var subQ1=sQuery(id+"F2.wireOp",EDGE,"E181");Q13=makeQuery(id+"F2.imprint","IMPRINT",FACE,{"disambiguationData":[TD([[makeQuery(id+"F2.imprint","IMPRINT",EDGE,{"derivedFrom":subQ1}),1.0]])]});}
            var Q14;
            {var subQ1=sQuery(id+"F2.wireOp",EDGE,"E182");Q14=makeQuery(id+"F2.imprint","IMPRINT",FACE,{"disambiguationData":[TD([[makeQuery(id+"F2.imprint","IMPRINT",EDGE,{"derivedFrom":subQ1}),1.0]])]});}
            var Q15;
            {var subQ1=sQuery(id+"F2.wireOp",EDGE,"E183");Q15=makeQuery(id+"F2.imprint","IMPRINT",FACE,{"disambiguationData":[TD([[makeQuery(id+"F2.imprint","IMPRINT",EDGE,{"derivedFrom":subQ1}),1.0]])]});}
            var Q16;
            {var subQ8=sQuery(id+"F2.wireOp",EDGE,"E255.1");Q16=makeQuery(id+"F2.imprint","IMPRINT",FACE,{"disambiguationData":[TD([[makeQuery(id+"F2.imprint","IMPRINT",EDGE,{"derivedFrom":subQ8}),1.0]])]});}
            var Q17;
            {var subQ2=sQuery(id+"F2.wireOp",EDGE,"E191");Q17=makeQuery(id+"F2.imprint","IMPRINT",FACE,{"disambiguationData":[TD([[makeQuery(id+"F2.imprint","IMPRINT",EDGE,{"derivedFrom":subQ2}),1.0]])]});}
            var Q18;
            {var subQ0=sQuery(id+"F2.wireOp",EDGE,"E189");Q18=makeQuery(id+"F2.imprint","IMPRINT",FACE,{"disambiguationData":[TD([[makeQuery(id+"F2.imprint","IMPRINT",EDGE,{"derivedFrom":subQ0}),-1.0]])]});}
            var Q19;
            {var subQ1=sQuery(id+"F2.wireOp",EDGE,"E184");Q19=makeQuery(id+"F2.imprint","IMPRINT",FACE,{"disambiguationData":[TD([[makeQuery(id+"F2.imprint","IMPRINT",EDGE,{"derivedFrom":subQ1}),1.0]])]});}
            extrude(context, id + "F4", {"entities" : qUnion([Q0, Q1, Q2, Q3, Q4, Q5, Q6, Q7, Q8, Q9, Q10, Q11, Q12, Q13, Q14, Q15, Q16, Q17, Q18, Q19]), "operationType" : NewBodyOperationType.ADD, "depth" : 1.6 * mm});
        }
        {
            var Q0;
            {var subQ2=sQuery(id+"F2.wireOp",EDGE,"E87.1");Q0=makeQuery(id+"F2.imprint","IMPRINT",FACE,{"disambiguationData":[TD([[makeQuery(id+"F2.imprint","IMPRINT",EDGE,{"derivedFrom":subQ2}),-1.0]])]});}
            var Q1;
            {var subQ2=sQuery(id+"F2.wireOp",EDGE,"E141.trimOffspring");Q1=makeQuery(id+"F2.imprint","IMPRINT",FACE,{"disambiguationData":[TD([[makeQuery(id+"F2.imprint","IMPRINT",EDGE,{"derivedFrom":subQ2}),1.0]])]});}
            var Q2;
            {var subQ2=sQuery(id+"F2.wireOp",EDGE,"E111.trimOffspring");Q2=makeQuery(id+"F2.imprint","IMPRINT",FACE,{"disambiguationData":[TD([[makeQuery(id+"F2.imprint","IMPRINT",EDGE,{"derivedFrom":subQ2}),1.0]])]});}
            var Q3;
            {var subQ2=sQuery(id+"F2.wireOp",EDGE,"E89.0");Q3=makeQuery(id+"F2.imprint","IMPRINT",FACE,{"disambiguationData":[TD([[makeQuery(id+"F2.imprint","IMPRINT",EDGE,{"derivedFrom":subQ2}),1.0]])]});}
            var Q4;
            {var subQ2=sQuery(id+"F2.wireOp",EDGE,"E109.trimOffspring");Q4=makeQuery(id+"F2.imprint","IMPRINT",FACE,{"disambiguationData":[TD([[makeQuery(id+"F2.imprint","IMPRINT",EDGE,{"derivedFrom":subQ2}),-1.0]])]});}
            var Q5;
            {var subQ1=sQuery(id+"F2.wireOp",EDGE,"E143.trimOffspring");Q5=makeQuery(id+"F2.imprint","IMPRINT",FACE,{"disambiguationData":[TD([[makeQuery(id+"F2.imprint","IMPRINT",EDGE,{"derivedFrom":subQ1}),1.0]])]});}
            var Q6;
            {var subQ2=sQuery(id+"F2.wireOp",EDGE,"E131.trimOffspring");Q6=makeQuery(id+"F2.imprint","IMPRINT",FACE,{"disambiguationData":[TD([[makeQuery(id+"F2.imprint","IMPRINT",EDGE,{"derivedFrom":subQ2}),-1.0]])]});}
            var Q7;
            {var subQ1=sQuery(id+"F2.wireOp",EDGE,"E145.trimOffspring");Q7=makeQuery(id+"F2.imprint","IMPRINT",FACE,{"disambiguationData":[TD([[makeQuery(id+"F2.imprint","IMPRINT",EDGE,{"derivedFrom":subQ1}),1.0]])]});}
            var Q8;
            {var subQ1=sQuery(id+"F2.wireOp",EDGE,"E133.trimOffspring");Q8=makeQuery(id+"F2.imprint","IMPRINT",FACE,{"disambiguationData":[TD([[makeQuery(id+"F2.imprint","IMPRINT",EDGE,{"derivedFrom":subQ1}),-1.0]])]});}
            var Q9;
            {var subQ1=sQuery(id+"F2.wireOp",EDGE,"E147.trimOffspring");Q9=makeQuery(id+"F2.imprint","IMPRINT",FACE,{"disambiguationData":[TD([[makeQuery(id+"F2.imprint","IMPRINT",EDGE,{"derivedFrom":subQ1}),1.0]])]});}
            var Q10;
            {var subQ1=sQuery(id+"F2.wireOp",EDGE,"E135.trimOffspring");Q10=makeQuery(id+"F2.imprint","IMPRINT",FACE,{"disambiguationData":[TD([[makeQuery(id+"F2.imprint","IMPRINT",EDGE,{"derivedFrom":subQ1}),-1.0]])]});}
            var Q11;
            {var subQ1=sQuery(id+"F2.wireOp",EDGE,"E149.trimOffspring");Q11=makeQuery(id+"F2.imprint","IMPRINT",FACE,{"disambiguationData":[TD([[makeQuery(id+"F2.imprint","IMPRINT",EDGE,{"derivedFrom":subQ1}),1.0]])]});}
            var Q12;
            {var subQ1=sQuery(id+"F2.wireOp",EDGE,"E137.trimOffspring");Q12=makeQuery(id+"F2.imprint","IMPRINT",FACE,{"disambiguationData":[TD([[makeQuery(id+"F2.imprint","IMPRINT",EDGE,{"derivedFrom":subQ1}),-1.0]])]});}
            var Q13;
            {var subQ1=sQuery(id+"F2.wireOp",EDGE,"E151.trimOffspring");Q13=makeQuery(id+"F2.imprint","IMPRINT",FACE,{"disambiguationData":[TD([[makeQuery(id+"F2.imprint","IMPRINT",EDGE,{"derivedFrom":subQ1}),1.0]])]});}
            var Q14;
            {var subQ2=sQuery(id+"F2.wireOp",EDGE,"E139.trimOffspring");Q14=makeQuery(id+"F2.imprint","IMPRINT",FACE,{"disambiguationData":[TD([[makeQuery(id+"F2.imprint","IMPRINT",EDGE,{"derivedFrom":subQ2}),-1.0]])]});}
            var Q15;
            {var subQ1=sQuery(id+"F2.wireOp",EDGE,"E205.trimOffspring");Q15=makeQuery(id+"F2.imprint","IMPRINT",FACE,{"disambiguationData":[TD([[makeQuery(id+"F2.imprint","IMPRINT",EDGE,{"derivedFrom":subQ1}),1.0]])]});}
            var Q16;
            {var subQ1=sQuery(id+"F2.wireOp",EDGE,"E193.trimOffspring");Q16=makeQuery(id+"F2.imprint","IMPRINT",FACE,{"disambiguationData":[TD([[makeQuery(id+"F2.imprint","IMPRINT",EDGE,{"derivedFrom":subQ1}),-1.0]])]});}
            var Q17;
            {var subQ1=sQuery(id+"F2.wireOp",EDGE,"E207.trimOffspring");Q17=makeQuery(id+"F2.imprint","IMPRINT",FACE,{"disambiguationData":[TD([[makeQuery(id+"F2.imprint","IMPRINT",EDGE,{"derivedFrom":subQ1}),1.0]])]});}
            var Q18;
            {var subQ0=sQuery(id+"F2.wireOp",EDGE,"E195.trimOffspring");Q18=makeQuery(id+"F2.imprint","IMPRINT",FACE,{"disambiguationData":[TD([[makeQuery(id+"F2.imprint","IMPRINT",EDGE,{"derivedFrom":subQ0}),-1.0]])]});}
            var Q19;
            {var subQ1=sQuery(id+"F2.wireOp",EDGE,"E209.trimOffspring");Q19=makeQuery(id+"F2.imprint","IMPRINT",FACE,{"disambiguationData":[TD([[makeQuery(id+"F2.imprint","IMPRINT",EDGE,{"derivedFrom":subQ1}),1.0]])]});}
            var Q20;
            {var subQ1=sQuery(id+"F2.wireOp",EDGE,"E197.trimOffspring");Q20=makeQuery(id+"F2.imprint","IMPRINT",FACE,{"disambiguationData":[TD([[makeQuery(id+"F2.imprint","IMPRINT",EDGE,{"derivedFrom":subQ1}),-1.0]])]});}
            var Q21;
            {var subQ1=sQuery(id+"F2.wireOp",EDGE,"E211.trimOffspring");Q21=makeQuery(id+"F2.imprint","IMPRINT",FACE,{"disambiguationData":[TD([[makeQuery(id+"F2.imprint","IMPRINT",EDGE,{"derivedFrom":subQ1}),1.0]])]});}
            var Q22;
            {var subQ1=sQuery(id+"F2.wireOp",EDGE,"E199.trimOffspring");Q22=makeQuery(id+"F2.imprint","IMPRINT",FACE,{"disambiguationData":[TD([[makeQuery(id+"F2.imprint","IMPRINT",EDGE,{"derivedFrom":subQ1}),-1.0]])]});}
            var Q23;
            {var subQ1=sQuery(id+"F2.wireOp",EDGE,"E213.trimOffspring");Q23=makeQuery(id+"F2.imprint","IMPRINT",FACE,{"disambiguationData":[TD([[makeQuery(id+"F2.imprint","IMPRINT",EDGE,{"derivedFrom":subQ1}),1.0]])]});}
            var Q24;
            {var subQ1=sQuery(id+"F2.wireOp",EDGE,"E201.trimOffspring");Q24=makeQuery(id+"F2.imprint","IMPRINT",FACE,{"disambiguationData":[TD([[makeQuery(id+"F2.imprint","IMPRINT",EDGE,{"derivedFrom":subQ1}),-1.0]])]});}
            var Q25;
            {var subQ1=sQuery(id+"F2.wireOp",EDGE,"E215.trimOffspring");Q25=makeQuery(id+"F2.imprint","IMPRINT",FACE,{"disambiguationData":[TD([[makeQuery(id+"F2.imprint","IMPRINT",EDGE,{"derivedFrom":subQ1}),1.0]])]});}
            var Q26;
            {var subQ1=sQuery(id+"F2.wireOp",EDGE,"E203.trimOffspring");Q26=makeQuery(id+"F2.imprint","IMPRINT",FACE,{"disambiguationData":[TD([[makeQuery(id+"F2.imprint","IMPRINT",EDGE,{"derivedFrom":subQ1}),-1.0]])]});}
            var Q27;
            {var subQ1=sQuery(id+"F2.wireOp",EDGE,"E231.trimOffspring");Q27=makeQuery(id+"F2.imprint","IMPRINT",FACE,{"disambiguationData":[TD([[makeQuery(id+"F2.imprint","IMPRINT",EDGE,{"derivedFrom":subQ1}),1.0]])]});}
            var Q28;
            {var subQ1=sQuery(id+"F2.wireOp",EDGE,"E217.trimOffspring");Q28=makeQuery(id+"F2.imprint","IMPRINT",FACE,{"disambiguationData":[TD([[makeQuery(id+"F2.imprint","IMPRINT",EDGE,{"derivedFrom":subQ1}),-1.0]])]});}
            var Q29;
            {var subQ1=sQuery(id+"F2.wireOp",EDGE,"E229.trimOffspring");Q29=makeQuery(id+"F2.imprint","IMPRINT",FACE,{"disambiguationData":[TD([[makeQuery(id+"F2.imprint","IMPRINT",EDGE,{"derivedFrom":subQ1}),1.0]])]});}
            var Q30;
            {var subQ1=sQuery(id+"F2.wireOp",EDGE,"E219.trimOffspring");Q30=makeQuery(id+"F2.imprint","IMPRINT",FACE,{"disambiguationData":[TD([[makeQuery(id+"F2.imprint","IMPRINT",EDGE,{"derivedFrom":subQ1}),-1.0]])]});}
            var Q31;
            {var subQ1=sQuery(id+"F2.wireOp",EDGE,"E227.trimOffspring");Q31=makeQuery(id+"F2.imprint","IMPRINT",FACE,{"disambiguationData":[TD([[makeQuery(id+"F2.imprint","IMPRINT",EDGE,{"derivedFrom":subQ1}),1.0]])]});}
            var Q32;
            {var subQ1=sQuery(id+"F2.wireOp",EDGE,"E221.trimOffspring");Q32=makeQuery(id+"F2.imprint","IMPRINT",FACE,{"disambiguationData":[TD([[makeQuery(id+"F2.imprint","IMPRINT",EDGE,{"derivedFrom":subQ1}),-1.0]])]});}
            var Q33;
            {var subQ1=sQuery(id+"F2.wireOp",EDGE,"E225.trimOffspring");Q33=makeQuery(id+"F2.imprint","IMPRINT",FACE,{"disambiguationData":[TD([[makeQuery(id+"F2.imprint","IMPRINT",EDGE,{"derivedFrom":subQ1}),1.0]])]});}
            var Q34;
            {var subQ2=sQuery(id+"F2.wireOp",EDGE,"E223.trimOffspring");Q34=makeQuery(id+"F2.imprint","IMPRINT",FACE,{"disambiguationData":[TD([[makeQuery(id+"F2.imprint","IMPRINT",EDGE,{"derivedFrom":subQ2}),-1.0]])]});}
            var Q35;
            {var subQ2=sQuery(id+"F2.wireOp",EDGE,"E89.1");Q35=makeQuery(id+"F2.imprint","IMPRINT",FACE,{"disambiguationData":[TD([[makeQuery(id+"F2.imprint","IMPRINT",EDGE,{"derivedFrom":subQ2}),1.0]])]});}
            extrude(context, id + "F5", {"entities" : qUnion([Q0, Q1, Q2, Q3, Q4, Q5, Q6, Q7, Q8, Q9, Q10, Q11, Q12, Q13, Q14, Q15, Q16, Q17, Q18, Q19, Q20, Q21, Q22, Q23, Q24, Q25, Q26, Q27, Q28, Q29, Q30, Q31, Q32, Q33, Q34, Q35]), "operationType" : NewBodyOperationType.ADD, "depth" : 0.7 * mm});
        }
        {
            var Q0;
            Q0=makeQuery(id+"F4.opExtrude","CAP_EDGE",EDGE,{"disambiguationData":[OSD([sQuery(id+"F2.wireOp",EDGE,"E238.0"),sQuery(id+"F2.wireOp",EDGE,"E238.1")])],"isStart":false});
            var Q1;
            Q1=makeQuery(id+"F4.opExtrude","CAP_EDGE",EDGE,{"disambiguationData":[OSD([sQuery(id+"F2.wireOp",EDGE,"E237.0"),sQuery(id+"F2.wireOp",EDGE,"E237.1")])],"isStart":false});
            var Q2;
            Q2=makeQuery(id+"F4.opExtrude","CAP_EDGE",EDGE,{"disambiguationData":[OSD([sQuery(id+"F2.wireOp",EDGE,"E240.0"),sQuery(id+"F2.wireOp",EDGE,"E240.1")])],"isStart":false});
            var Q3;
            Q3=makeQuery(id+"F4.opExtrude","CAP_EDGE",EDGE,{"disambiguationData":[OSD([sQuery(id+"F2.wireOp",EDGE,"E239.0"),sQuery(id+"F2.wireOp",EDGE,"E239.1")])],"isStart":false});
            var Q4;
            Q4=makeQuery(id+"F4.opExtrude","CAP_EDGE",EDGE,{"disambiguationData":[OSD([sQuery(id+"F2.wireOp",EDGE,"E92.0"),sQuery(id+"F2.wireOp",EDGE,"E92.1")])],"isStart":false});
            var Q5;
            Q5=makeQuery(id+"F4.opExtrude","CAP_EDGE",EDGE,{"disambiguationData":[OSD([sQuery(id+"F2.wireOp",EDGE,"E249.trimOffspring")])],"isStart":false});
            var Q6;
            Q6=makeQuery(id+"F4.opExtrude","CAP_EDGE",EDGE,{"disambiguationData":[OSD([sQuery(id+"F2.wireOp",EDGE,"E107.trimOffspring")])],"isStart":false});
            var Q7;
            Q7=makeQuery(id+"F4.opExtrude","CAP_EDGE",EDGE,{"disambiguationData":[OSD([sQuery(id+"F2.wireOp",EDGE,"E91.0"),sQuery(id+"F2.wireOp",EDGE,"E91.1")])],"isStart":false});
            var Q8;
            Q8=makeQuery(id+"F4.opExtrude","CAP_EDGE",EDGE,{"disambiguationData":[OSD([sQuery(id+"F2.wireOp",EDGE,"E247.trimOffspring")])],"isStart":false});
            var Q9;
            Q9=makeQuery(id+"F4.opExtrude","CAP_EDGE",EDGE,{"disambiguationData":[OSD([sQuery(id+"F2.wireOp",EDGE,"E253.trimOffspring")])],"isStart":false});
            var Q10;
            Q10=makeQuery(id+"F4.opExtrude","CAP_EDGE",EDGE,{"disambiguationData":[OSD([sQuery(id+"F2.wireOp",EDGE,"E248.trimOffspring")])],"isStart":false});
            var Q11;
            Q11=makeQuery(id+"F4.opExtrude","CAP_EDGE",EDGE,{"disambiguationData":[OSD([sQuery(id+"F2.wireOp",EDGE,"E94.0"),sQuery(id+"F2.wireOp",EDGE,"E94.1")])],"isStart":false});
            var Q12;
            Q12=makeQuery(id+"F4.opExtrude","CAP_EDGE",EDGE,{"disambiguationData":[OSD([sQuery(id+"F2.wireOp",EDGE,"E108.trimOffspring")])],"isStart":false});
            var Q13;
            Q13=makeQuery(id+"F4.opExtrude","CAP_EDGE",EDGE,{"disambiguationData":[OSD([sQuery(id+"F2.wireOp",EDGE,"E93.0"),sQuery(id+"F2.wireOp",EDGE,"E93.1")])],"isStart":false});
            var Q14;
            Q14=makeQuery(id+"F4.opExtrude","CAP_EDGE",EDGE,{"disambiguationData":[OSD([sQuery(id+"F2.wireOp",EDGE,"E114.0"),sQuery(id+"F2.wireOp",EDGE,"E114.1")])],"isStart":false});
            var Q15;
            Q15=makeQuery(id+"F4.opExtrude","CAP_EDGE",EDGE,{"disambiguationData":[OSD([sQuery(id+"F2.wireOp",EDGE,"E113.0"),sQuery(id+"F2.wireOp",EDGE,"E113.1")])],"isStart":false});
            var Q16;
            Q16=makeQuery(id+"F4.opExtrude","CAP_EDGE",EDGE,{"disambiguationData":[OSD([sQuery(id+"F2.wireOp",EDGE,"E116.0"),sQuery(id+"F2.wireOp",EDGE,"E116.1")])],"isStart":false});
            var Q17;
            Q17=makeQuery(id+"F4.opExtrude","CAP_EDGE",EDGE,{"disambiguationData":[OSD([sQuery(id+"F2.wireOp",EDGE,"E115.0"),sQuery(id+"F2.wireOp",EDGE,"E115.1")])],"isStart":false});
            var Q18;
            Q18=makeQuery(id+"F4.opExtrude","CAP_EDGE",EDGE,{"disambiguationData":[OSD([sQuery(id+"F2.wireOp",EDGE,"E118.0"),sQuery(id+"F2.wireOp",EDGE,"E118.1")])],"isStart":false});
            var Q19;
            Q19=makeQuery(id+"F4.opExtrude","CAP_EDGE",EDGE,{"disambiguationData":[OSD([sQuery(id+"F2.wireOp",EDGE,"E117.0"),sQuery(id+"F2.wireOp",EDGE,"E117.1")])],"isStart":false});
            var Q20;
            Q20=makeQuery(id+"F4.opExtrude","CAP_EDGE",EDGE,{"disambiguationData":[OSD([sQuery(id+"F2.wireOp",EDGE,"E259.1")])],"isStart":false});
            var Q21;
            Q21=makeQuery(id+"F4.opExtrude","CAP_EDGE",EDGE,{"disambiguationData":[OSD([sQuery(id+"F2.wireOp",EDGE,"E259.0")])],"isStart":false});
            var Q22;
            Q22=makeQuery(id+"F4.opExtrude","CAP_EDGE",EDGE,{"disambiguationData":[OSD([sQuery(id+"F2.wireOp",EDGE,"E260.1")])],"isStart":false});
            var Q23;
            Q23=makeQuery(id+"F4.opExtrude","CAP_EDGE",EDGE,{"disambiguationData":[OSD([sQuery(id+"F2.wireOp",EDGE,"E260.0")])],"isStart":false});
            var Q24;
            Q24=makeQuery(id+"F4.opExtrude","CAP_EDGE",EDGE,{"disambiguationData":[OSD([sQuery(id+"F2.wireOp",EDGE,"E120.0"),sQuery(id+"F2.wireOp",EDGE,"E120.1")])],"isStart":false});
            var Q25;
            Q25=makeQuery(id+"F4.opExtrude","CAP_EDGE",EDGE,{"disambiguationData":[OSD([sQuery(id+"F2.wireOp",EDGE,"E119.0"),sQuery(id+"F2.wireOp",EDGE,"E119.1")])],"isStart":false});
            var Q26;
            Q26=makeQuery(id+"F4.opExtrude","CAP_EDGE",EDGE,{"disambiguationData":[OSD([sQuery(id+"F2.wireOp",EDGE,"E154.0"),sQuery(id+"F2.wireOp",EDGE,"E154.1")])],"isStart":false});
            var Q27;
            Q27=makeQuery(id+"F4.opExtrude","CAP_EDGE",EDGE,{"disambiguationData":[OSD([sQuery(id+"F2.wireOp",EDGE,"E153.0"),sQuery(id+"F2.wireOp",EDGE,"E153.1")])],"isStart":false});
            var Q28;
            Q28=makeQuery(id+"F4.opExtrude","CAP_EDGE",EDGE,{"disambiguationData":[OSD([sQuery(id+"F2.wireOp",EDGE,"E156.0"),sQuery(id+"F2.wireOp",EDGE,"E156.1")])],"isStart":false});
            var Q29;
            Q29=makeQuery(id+"F4.opExtrude","CAP_EDGE",EDGE,{"disambiguationData":[OSD([sQuery(id+"F2.wireOp",EDGE,"E155.0"),sQuery(id+"F2.wireOp",EDGE,"E155.1")])],"isStart":false});
            var Q30;
            Q30=makeQuery(id+"F4.opExtrude","CAP_EDGE",EDGE,{"disambiguationData":[OSD([sQuery(id+"F2.wireOp",EDGE,"E158.0"),sQuery(id+"F2.wireOp",EDGE,"E158.1")])],"isStart":false});
            var Q31;
            Q31=makeQuery(id+"F4.opExtrude","CAP_EDGE",EDGE,{"disambiguationData":[OSD([sQuery(id+"F2.wireOp",EDGE,"E157.0"),sQuery(id+"F2.wireOp",EDGE,"E157.1")])],"isStart":false});
            var Q32;
            Q32=makeQuery(id+"F4.opExtrude","CAP_EDGE",EDGE,{"disambiguationData":[OSD([sQuery(id+"F2.wireOp",EDGE,"E160.0"),sQuery(id+"F2.wireOp",EDGE,"E160.1")])],"isStart":false});
            var Q33;
            Q33=makeQuery(id+"F4.opExtrude","CAP_EDGE",EDGE,{"disambiguationData":[OSD([sQuery(id+"F2.wireOp",EDGE,"E159.0"),sQuery(id+"F2.wireOp",EDGE,"E159.1")])],"isStart":false});
            var Q34;
            Q34=makeQuery(id+"F4.opExtrude","CAP_EDGE",EDGE,{"disambiguationData":[OSD([sQuery(id+"F2.wireOp",EDGE,"E162.0"),sQuery(id+"F2.wireOp",EDGE,"E162.1")])],"isStart":false});
            var Q35;
            Q35=makeQuery(id+"F4.opExtrude","CAP_EDGE",EDGE,{"disambiguationData":[OSD([sQuery(id+"F2.wireOp",EDGE,"E161.0"),sQuery(id+"F2.wireOp",EDGE,"E161.1")])],"isStart":false});
            var Q36;
            Q36=makeQuery(id+"F4.opExtrude","CAP_EDGE",EDGE,{"disambiguationData":[OSD([sQuery(id+"F2.wireOp",EDGE,"E164.0"),sQuery(id+"F2.wireOp",EDGE,"E164.1")])],"isStart":false});
            var Q37;
            Q37=makeQuery(id+"F4.opExtrude","CAP_EDGE",EDGE,{"disambiguationData":[OSD([sQuery(id+"F2.wireOp",EDGE,"E163.0"),sQuery(id+"F2.wireOp",EDGE,"E163.1")])],"isStart":false});
            var Q38;
            Q38=makeQuery(id+"F4.opExtrude","CAP_EDGE",EDGE,{"disambiguationData":[OSD([sQuery(id+"F2.wireOp",EDGE,"E166.0"),sQuery(id+"F2.wireOp",EDGE,"E166.1")])],"isStart":false});
            var Q39;
            Q39=makeQuery(id+"F4.opExtrude","CAP_EDGE",EDGE,{"disambiguationData":[OSD([sQuery(id+"F2.wireOp",EDGE,"E165.0"),sQuery(id+"F2.wireOp",EDGE,"E165.1")])],"isStart":false});
            var Q40;
            Q40=makeQuery(id+"F4.opExtrude","CAP_EDGE",EDGE,{"disambiguationData":[OSD([sQuery(id+"F2.wireOp",EDGE,"E168.0")])],"isStart":false});
            var Q41;
            Q41=makeQuery(id+"F4.opExtrude","CAP_EDGE",EDGE,{"disambiguationData":[OSD([sQuery(id+"F2.wireOp",EDGE,"E168.1")])],"isStart":false});
            var Q42;
            Q42=makeQuery(id+"F4.opExtrude","CAP_EDGE",EDGE,{"disambiguationData":[OSD([sQuery(id+"F2.wireOp",EDGE,"E167.0")])],"isStart":false});
            var Q43;
            Q43=makeQuery(id+"F4.opExtrude","CAP_EDGE",EDGE,{"disambiguationData":[OSD([sQuery(id+"F2.wireOp",EDGE,"E167.1")])],"isStart":false});
            var Q44;
            Q44=makeQuery(id+"F4.opExtrude","CAP_EDGE",EDGE,{"disambiguationData":[OSD([sQuery(id+"F2.wireOp",EDGE,"E170.0"),sQuery(id+"F2.wireOp",EDGE,"E170.1")])],"isStart":false});
            var Q45;
            Q45=makeQuery(id+"F4.opExtrude","CAP_EDGE",EDGE,{"disambiguationData":[OSD([sQuery(id+"F2.wireOp",EDGE,"E169.0"),sQuery(id+"F2.wireOp",EDGE,"E169.1")])],"isStart":false});
            var Q46;
            Q46=makeQuery(id+"F4.opExtrude","CAP_EDGE",EDGE,{"disambiguationData":[OSD([sQuery(id+"F2.wireOp",EDGE,"E172.0"),sQuery(id+"F2.wireOp",EDGE,"E172.1")])],"isStart":false});
            var Q47;
            Q47=makeQuery(id+"F4.opExtrude","CAP_EDGE",EDGE,{"disambiguationData":[OSD([sQuery(id+"F2.wireOp",EDGE,"E171.0"),sQuery(id+"F2.wireOp",EDGE,"E171.1")])],"isStart":false});
            var Q48;
            Q48=makeQuery(id+"F4.opExtrude","CAP_EDGE",EDGE,{"disambiguationData":[OSD([sQuery(id+"F2.wireOp",EDGE,"E255.2"),sQuery(id+"F2.wireOp",EDGE,"E255.3")])],"isStart":false});
            var Q49;
            Q49=makeQuery(id+"F4.opExtrude","CAP_EDGE",EDGE,{"disambiguationData":[OSD([sQuery(id+"F2.wireOp",EDGE,"E255.0"),sQuery(id+"F2.wireOp",EDGE,"E255.1")])],"isStart":false});
            var Q50;
            Q50=makeQuery(id+"F4.opExtrude","CAP_EDGE",EDGE,{"disambiguationData":[OSD([sQuery(id+"F2.wireOp",EDGE,"E256.0"),sQuery(id+"F2.wireOp",EDGE,"E256.1")])],"isStart":false});
            var Q51;
            Q51=makeQuery(id+"F4.opExtrude","CAP_EDGE",EDGE,{"disambiguationData":[OSD([sQuery(id+"F2.wireOp",EDGE,"E256.2"),sQuery(id+"F2.wireOp",EDGE,"E256.3")])],"isStart":false});
            chamfer(context, id + "F6", {"entities" : qUnion([Q0, Q1, Q2, Q3, Q4, Q5, Q6, Q7, Q8, Q9, Q10, Q11, Q12, Q13, Q14, Q15, Q16, Q17, Q18, Q19, Q20, Q21, Q22, Q23, Q24, Q25, Q26, Q27, Q28, Q29, Q30, Q31, Q32, Q33, Q34, Q35, Q36, Q37, Q38, Q39, Q40, Q41, Q42, Q43, Q44, Q45, Q46, Q47, Q48, Q49, Q50, Q51]), "width" : 0.1 * mm});
        }
    });
